# Revit family: QF_BOURGEAT_Satellite4G_GN3_pied_inox_chaud_et_froid
name_source: partatom
category: Equipement spécialisé
revit_build: Autodesk Revit 2015 (Build: 20140606_1530(x64)
units: mm (PartAtom-declared; Revit-internal decimal feet)

## types (2) — shared parameters
Certification = NF hygiene alimentaire
Charge max = 30.00 kg
Diametre_roue = 80 mm  [stored 0.262467 ft]
Fabricant = BOURGEAT
Fréquence = 50 Hz
Hauteur hors tout = 688 mm  [stored 2.25722 ft]
Hauteur_poignee_porte_sol = 280 mm  [stored 0.918635 ft]
Hauteur_poignees_laterales = 791 mm
Hauteur_porte = 541 mm
Hauteur_roue = 107 mm  [stored 0.35105 ft]
Indice de protection = IP25
Largeur_porte = 706 mm  [stored 2.31627 ft]
Longueur hors tout = 752 mm  [stored 2.46719 ft]
Materiau_Poignee_porte = B_Elastomère_TPE_S
Materiau_bac = Acier inoxydable, brossé
Materiau_bandage = B_Elastomère_TPE_S
Materiau_porte = Acier inoxydable, brossé
Materiau_vitre = Verre, vitrage transparent, trempé
Nature isolant = Mousse sans PU
Phase = 2
Poignee_droite = Oui
Poignee_gauche = Non
Pos_V_IHM = 38 mm  [stored 0.124672 ft]
Spécification du Fabricant = Satellite 4G
Tension = 230 V
URL catalogue = http://www.bourgeat.fr

## per-type parameters (varying)
| type | Charge_gaz | Classe Climatique | Consommation énergétique | Intensité nominale | Longueur_poignees_laterales | Modèle | Poids net à vide | Profondeur hors tout | Puissance frigorifique | Puissance électrique  | Type Fluide Frigorigène |
| GN3_chaud |  |  | 0.15Kwh/h NFD40-016 | 4 A | 420 mm  [stored 1.37795 ft] | 843402 | 60.00 kg | 576 mm  [stored 1.88976 ft] |  | 950 W |  |
| GN3_froid | 0.150Kg | 4 | 2.4Kwh/h NFD40-016 | 1 A | 571 mm  [stored 1.87336 ft] | 842404 | 75.00 kg | 727 mm  [stored 2.38517 ft] | 270w à-5°C | 300 W | R134a |

note: [stored X ft] marks values corroborated as IEEE doubles in the binary element streams (Revit-internal decimal feet)
